# Revit family: WBY_A3-Bay-2707x2107-BW2106-18-06
name_source: partatom
category: Windows
revit_build: Autodesk Revit 2016 (Build: 20150220_1215(x64)
units: mm (PartAtom-declared; Revit-internal decimal feet)

## family parameters
Always vertical = Yes
Cut with Voids When Loaded = No
Host = Wall
Room Calculation Point = No
Shared = No

## types (1)
- 2707 x 2107 BW2106 18 06
    Assembly Code = B2020100
    Frame Material = Kiln Dried Wood
    Frame Thickness = 90 mm  [stored 0.295276 ft]
    Glass Material = Glass
    Glass Thickness = 8 mm  [stored 0.0262467 ft]
    Head Height = 2300 mm
    Height = 2107 mm
    Manufacturer = Caterbury
    Manufacturer Code = BW2106 18 06
    Model = Bay Window
    Offset = 41 mm  [stored 0.134514 ft]
    Panel Thickness = 40 mm  [stored 0.131234 ft]
    URL = www.canterbury.com.au
    Wall Closure = By host
    Width = 2707 mm  [stored 8.88123 ft]
    half = 45 mm  [stored 0.147638 ft]

note: [stored X ft] marks values corroborated as IEEE doubles in the binary element streams (Revit-internal decimal feet)

## geometry (parser evidence)
native form markers: Sweep x1
no freeform markers — native parametric forms only
